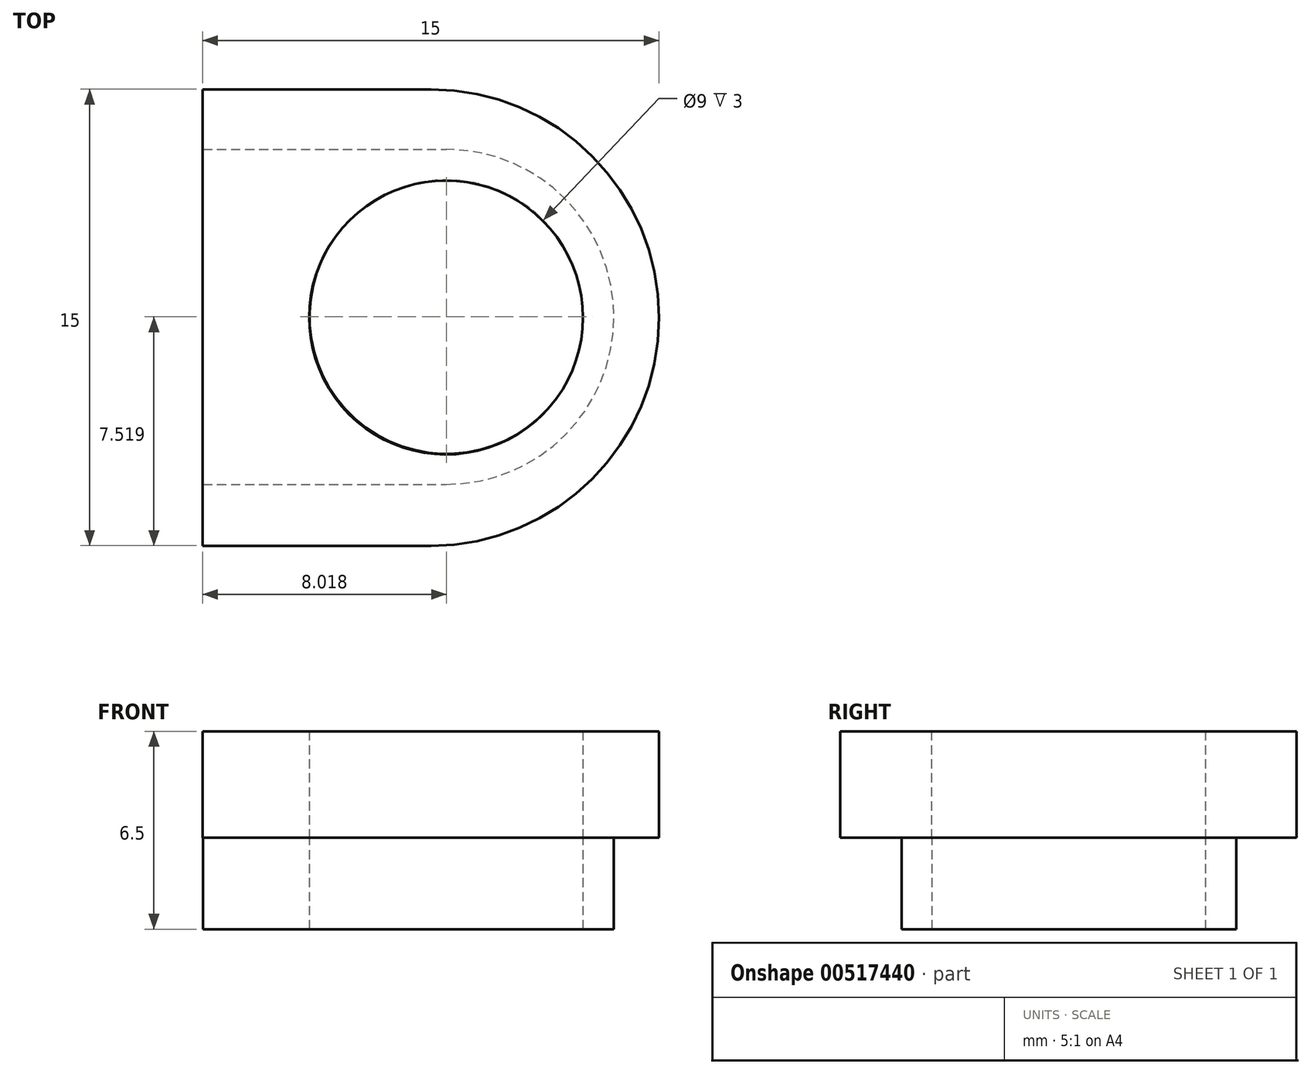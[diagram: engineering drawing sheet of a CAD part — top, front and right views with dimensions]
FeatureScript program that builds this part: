
annotation { "Feature Type Name" : "Feature", "Feature Type Description" : "" }
export const myFeature = defineFeature(function(context is Context, id is Id, definition is map)
    precondition{}
    {
        {
            var Q0;
            Q0=qCreatedBy(makeId("Top.planeOp"),FACE);
            var sketch = newSketch(context, id + "F0", { "sketchPlane" : qUnion([Q0])});
            skLineSegment(sketch, "E0.bottom", {"start": v(-48.58, 41.94) * mm, "end": v(-41.08, 41.94) * mm});
            skLineSegment(sketch, "E0.top", {"start": v(-48.58, 26.94) * mm, "end": v(-41.08, 26.94) * mm});
            skLineSegment(sketch, "E0.left", {"start": v(-48.58, 41.94) * mm, "end": v(-48.58, 26.94) * mm});
            skLineSegment(sketch, "E0.right", {"start": v(-41.08, 41.94) * mm, "end": v(-41.08, 26.94) * mm});
            skCircle(sketch, "E1", {"center": v(-40.58, 34.44) * mm, "radius": 4.5 * mm});
            skArc(sketch, "E2", {"start": v(-41.08, 26.94) * mm, "mid": v(-33.58, 34.44) * mm, "end": v(-41.08, 41.94) * mm});
            skSolve(sketch);
        }
        {
            var Q0;
            Q0 = qSketchRegion(id + "F0", true);
            extrude(context, id + "F1", {"entities" : qUnion([Q0]), "depth" : 3.5 * mm, "offsetDistance" : 25 * mm});
        }
        {
            var Q0;
            Q0=qCreatedBy(makeId("Top.planeOp"),FACE);
            var sketch = newSketch(context, id + "F2", { "sketchPlane" : qUnion([Q0])});
            skLineSegment(sketch, "E3.bottom", {"start": v(-48.56, 39.96) * mm, "end": v(-40.56, 39.96) * mm});
            skLineSegment(sketch, "E3.top", {"start": v(-48.56, 28.96) * mm, "end": v(-40.56, 28.96) * mm});
            skLineSegment(sketch, "E3.left", {"start": v(-48.56, 39.96) * mm, "end": v(-48.56, 28.96) * mm});
            skLineSegment(sketch, "E3.right", {"start": v(-40.56, 39.96) * mm, "end": v(-40.56, 28.96) * mm});
            skCircle(sketch, "E4", {"center": v(-40.56, 34.46) * mm, "radius": 4.5 * mm});
            skArc(sketch, "E5", {"start": v(-40.56, 28.96) * mm, "mid": v(-35.06, 34.46) * mm, "end": v(-40.56, 39.96) * mm});
            skSolve(sketch);
        }
        {
            var Q0;
            Q0 = qSketchRegion(id + "F2", true);
            extrude(context, id + "F3", {"entities" : qUnion([Q0]), "operationType" : NewBodyOperationType.ADD, "oppositeDirection" : true, "depth" : 3 * mm, "offsetDistance" : 25 * mm});
        }
    });
